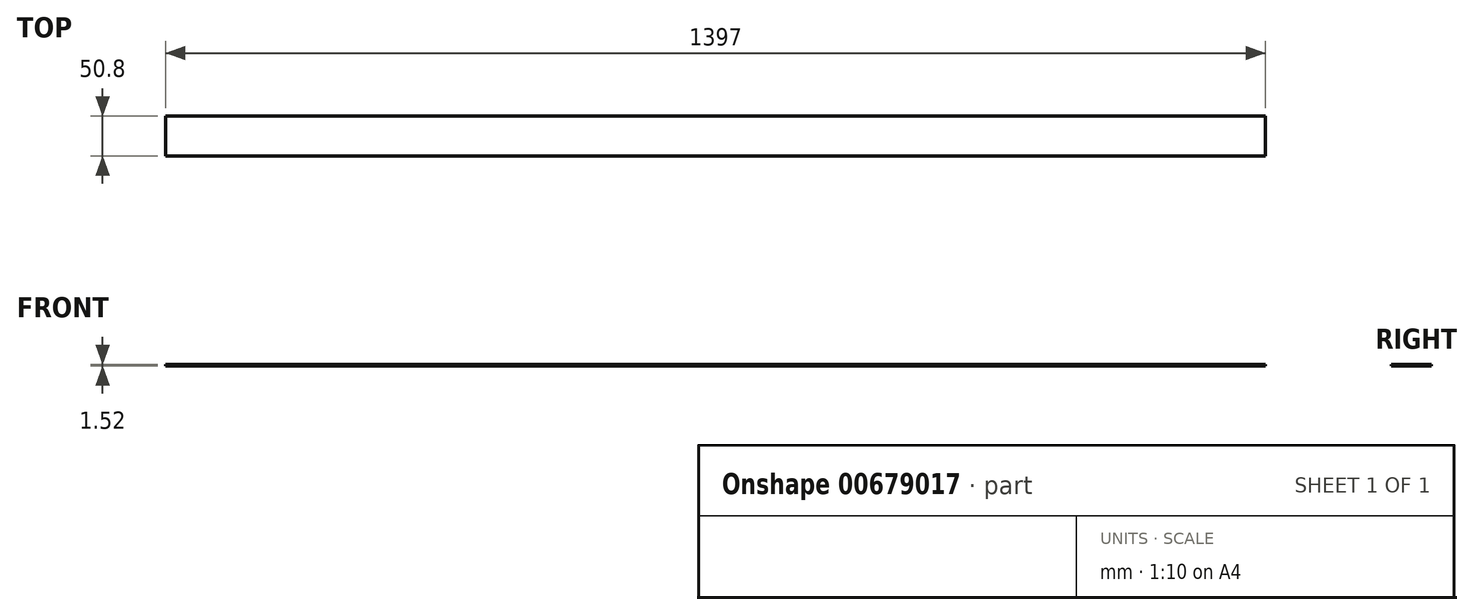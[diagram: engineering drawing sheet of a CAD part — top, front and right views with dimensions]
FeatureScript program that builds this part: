
annotation { "Feature Type Name" : "Feature", "Feature Type Description" : "" }
export const myFeature = defineFeature(function(context is Context, id is Id, definition is map)
    precondition{}
    {
        {
            var Q0;
            Q0=qCreatedBy(makeId("Top.planeOp"),FACE);
            var sketch = newSketch(context, id + "F0", { "sketchPlane" : qUnion([Q0])});
            skLineSegment(sketch, "E0.bottom", {"start": v(-698.5, 25.4) * mm, "end": v(698.5, 25.4) * mm});
            skLineSegment(sketch, "E0.top", {"start": v(-698.5, -25.4) * mm, "end": v(698.5, -25.4) * mm});
            skLineSegment(sketch, "E0.left", {"start": v(-698.5, 25.4) * mm, "end": v(-698.5, -25.4) * mm});
            skLineSegment(sketch, "E0.right", {"start": v(698.5, 25.4) * mm, "end": v(698.5, -25.4) * mm});
            skPoint(sketch, "E0.middle", {"position": v(0, 0) * mm});
            skSolve(sketch);
        }
        {
            var Q0;
            Q0=makeQuery(id+"F0.imprint","IMPRINT",FACE,{"disambiguationData":[TD([[makeQuery(id+"F0.imprint","IMPRINT",EDGE,{"derivedFrom":sQuery(id+"F0.wireOp",EDGE,"E0.bottom")}),-1.0]])]});
            extrude(context, id + "F1", {"entities" : qUnion([Q0]), "depth" : 1.52 * mm, "offsetDistance" : 25.4 * mm});
        }
    });
